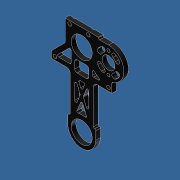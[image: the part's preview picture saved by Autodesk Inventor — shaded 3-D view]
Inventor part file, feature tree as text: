
AUTODESK INVENTOR PART (.ipt)
format: ipt  version: unknown  size: 564,224 bytes
history: native  units: in
note: dims shown in document units (in); Inventor stores cm internally (conversion verified against a paired STEP export)
features: sketch x19, extrude x16, fillet x8, hole x3, pattern_circular x1, projected_geometry x1, reference x1
ambient origin geometry x8: Origin, YZ Plane, XZ Plane, XY Plane, X Axis, Y Axis, Z Axis, Center Point
bodies: Solid1 (feature_tree)
feature tree (49):
  extrude  "Extrusion1"  Depth=3.5in
  extrude  "Extrusion2"  Depth=1.25in
  extrude  "Extrusion3"  Depth=1.125in
  extrude  "Extrusion4"  Depth=3.25in
  extrude  "Extrusion5"  Depth=1.124in
  extrude  "Extrusion8"  Depth=0.625in
  extrude  "Extrusion7"  Depth=0.125in
  hole  "Hole1"  [1 undecoded]
  hole  "Hole2"  [1 undecoded]
  extrude  "Extrusion9"  Depth=1.0in TaperAngle=0.0deg
  fillet  "Fillet2"  Radius=1.4375in
  extrude  "Extrusion10"  Depth=1.325in
  extrude  "Extrusion12"  Depth=0.378in
  pattern_circular  "Circular Pattern1"  [2 undecoded]
  fillet  "Fillet8"  Radius=0.1875in
  extrude  "Extrusion13"  Depth=0.1812in
  hole  "Hole3"  [1 undecoded]
  extrude  "Extrusion14"  Depth=0.1812in
  extrude  "Extrusion17"  Depth=2.375in
  extrude  "Extrusion18"  Depth=0.125in
  extrude  "Extrusion19"  Depth=0.125in
  fillet  "Fillet15"  Radius=0.125in
  fillet  "Fillet16"  Radius=2.375in
  fillet  "Fillet17"  Radius=0.25in
  fillet  "Fillet18"  Radius=0.75in
  extrude  "Extrusion20"  Depth=1.65in
  fillet  "Fillet19"  Radius=0.25in
  fillet  "Fillet20"  Radius=0.875in
  sketch  "Sketch1"  dims[d0=5.5in d1=3.5in]
  sketch  "Sketch2"  dims[d2=0.25in d3=0.0in d4=1.25in]
  sketch  "Sketch3"  dims[d5=1.125in d6=1.125in]
  sketch  "Sketch4"  dims[d7=3.25in d8=3.25in]
  sketch  "Sketch5"  dims[d9=0.25in d10=0.0in d11=1.124in]
  sketch  "Sketch7"  dims[d12=0.625in d13=0.625in]
  sketch  "Sketch8"  dims[d14=1.0in d15=0.0in d16=0.125in]
  sketch  "Sketch9"  dims[d17=0.125in d18=1.0in d19=0.0in]
  sketch  "Sketch10"  dims[d20=1.325in d21=1.625in]
  sketch  "Sketch11"  dims[d22=1.124in d23=1.0in d24=0.0in d27=1.4375in]
  sketch  "Sketch12"  dims[d28=0.6875in d31=1.325in]
  sketch  "Sketch14"  dims[d32=1.0in d33=0.0in d34=0.378in]
  sketch  "Sketch15"  dims[d35=0.378in]
  sketch  "Sketch16"  dims[d36=1.75in]
  sketch  "Sketch17"  dims[d37=0.25in d38=0.0in]
  projected_geometry  "Projected Loop1"
  sketch  "Sketch20"  dims[d39=0.5709in]
  sketch  "Sketch21"  dims[d40=0.5709in]
  reference  "Reference1"
  sketch  "Sketch22"  dims[d41=0.5655in]
  sketch  "Sketch23"  dims[d42=0.5655in d43=0.5655in d44=0.169in d45=0.75in d46=0.37in d47=0.25in d48=90.0deg d49=1.0in d50=0.8108in d51=0.1875in d52=0.1812in d53=0.1875in d54=0.1812in d55=0.196in d56=0.75in d57=0.385in d58=0.25in d59=0.5635in d60=1.0in d61=0.8108in d62=2.375in d63=0.125in d64=0.125in d65=0.125in d66=2.375in d67=0.25in d68=0.0in d70=0.75in d81=1.65in d83=0.25in d84=0.0in d90=0.875in d92=0.25in d93=0.1374in d94=0.481in d95=0.1374in d96=0.481in d97=0.3698in d98=0.25in d99=0.0in d100=1.5748in d101=360.0deg d103=0.125in d104=0.3625in d105=0.726in d106=0.25in d107=0.0in d109=0.1625in d110=0.1625in d111=0.25in d112=1.0in d113=0.196in d114=0.75in d115=0.385in d116=0.25in d117=0.5635in d118=1.0in d119=0.8108in d120=1.798in d121=0.25in d122=0.0in d164=45.0deg d165=0.25in d166=0.0in d167=0.25in d168=0.0in d170=0.625in d171=0.75in d172=1.25in d173=1.625in d174=1.0in d175=0.0in d176=0.125in d177=0.0625in d178=0.0625in d179=0.0625in d180=0.5in d181=0.5in d182=1.0in d183=0.0in d184=0.0625in d185=0.1875in]
note: 5 required parameter values undecoded (feature->parameter linkage not recoverable at this tier; creation-order binding heuristic only, values carry confidence <= 0.55)
